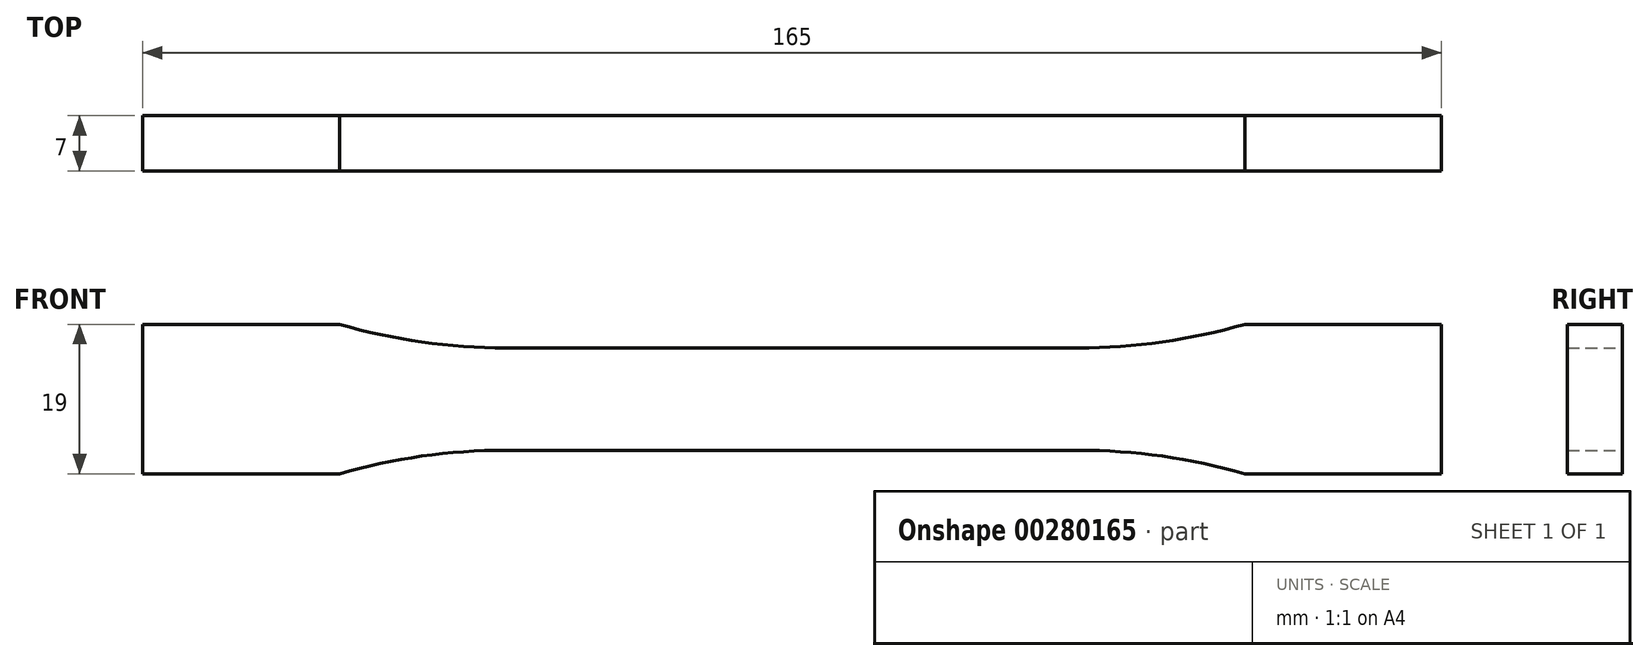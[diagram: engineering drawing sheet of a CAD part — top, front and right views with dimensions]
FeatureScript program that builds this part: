
annotation { "Feature Type Name" : "Feature", "Feature Type Description" : "" }
export const myFeature = defineFeature(function(context is Context, id is Id, definition is map)
    precondition{}
    {
        {
            var Q0;
            Q0=qCreatedBy(makeId("Front.planeOp"),FACE);
            var sketch = newSketch(context, id + "F0", { "sketchPlane" : qUnion([Q0])});
            skLineSegment(sketch, "E0", {"start": v(0, 6.5) * mm, "end": v(36.36, 6.5) * mm});
            skArc(sketch, "E1", {"start": v(36.36, 6.5) * mm, "mid": v(47.03, 7.25) * mm, "end": v(57.5, 9.5) * mm});
            skLineSegment(sketch, "E2", {"start": v(57.5, 9.5) * mm, "end": v(82.5, 9.5) * mm});
            skLineSegment(sketch, "E3.MirrorCS", {"start": v(57.5, -9.5) * mm, "end": v(82.5, -9.5) * mm});
            skLineSegment(sketch, "E4.MirrorCS", {"start": v(0, -6.5) * mm, "end": v(36.36, -6.5) * mm});
            skArc(sketch, "E5.MirrorCS", {"start": v(36.36, -6.5) * mm, "mid": v(47.03, -7.25) * mm, "end": v(57.5, -9.5) * mm});
            skArc(sketch, "E6.MirrorCS", {"start": v(-36.36, -6.5) * mm, "mid": v(-47.03, -7.25) * mm, "end": v(-57.5, -9.5) * mm});
            skLineSegment(sketch, "E7.MirrorCS", {"start": v(0, 6.5) * mm, "end": v(-36.36, 6.5) * mm});
            skArc(sketch, "E8.MirrorCS", {"start": v(-36.36, 6.5) * mm, "mid": v(-47.03, 7.25) * mm, "end": v(-57.5, 9.5) * mm});
            skLineSegment(sketch, "E9.MirrorCS", {"start": v(-57.5, -9.5) * mm, "end": v(-82.5, -9.5) * mm});
            skLineSegment(sketch, "E10.MirrorCS", {"start": v(0, -6.5) * mm, "end": v(-36.36, -6.5) * mm});
            skLineSegment(sketch, "E11.MirrorCS", {"start": v(-57.5, 9.5) * mm, "end": v(-82.5, 9.5) * mm});
            skLineSegment(sketch, "E12", {"start": v(82.5, 9.5) * mm, "end": v(82.5, -9.5) * mm});
            skLineSegment(sketch, "E13", {"start": v(-82.5, 9.5) * mm, "end": v(-82.5, -9.5) * mm});
            skSolve(sketch);
        }
        {
            var Q0;
            Q0=makeQuery(id+"F0.imprint","IMPRINT",FACE,{"disambiguationData":[TD([[makeQuery(id+"F0.imprint","IMPRINT",EDGE,{"derivedFrom":sQuery(id+"F0.wireOp",EDGE,"E0")}),-1.0]])]});
            extrude(context, id + "F1", {"entities" : qUnion([Q0]), "endBound" : BoundingType.SYMMETRIC, "depth" : 7 * mm});
        }
    });
